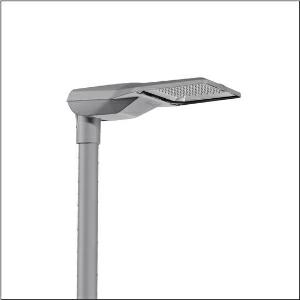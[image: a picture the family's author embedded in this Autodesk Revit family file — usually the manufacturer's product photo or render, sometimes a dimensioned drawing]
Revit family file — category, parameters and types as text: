
# Revit family: streetlight_sl_21_iq_midi___st0_8a_5xe3c31g08nb_0abe
name_source: partatom
category: Lighting Fixtures
units: mm (PartAtom-declared; Revit-internal decimal feet)

## family parameters
Cut with Voids When Loaded = No
Host = Face
Light Source = No
Part Type = Normal
Room Calculation Point = No
Round Connector Dimension = Use Diameter
Shared = No

## types (1)
- --- (1 x LED, 23230 lm, 155.5 W, 3000K)
    Apparent Load = 155 VA
    CIE Flux Codes = 41 75 97 100 100
    Color Rendering = 70
    Color Temperature = 3000K
    Default Elevation = 1800 mm
    Description = Streetlight SL 21 iQ midi, mast luminaire, primary light control with lens, of PMMA, primary optical cover: cover, of toughened safety glass, transparent, light distribution: ST0.8a, light emission: direct distribution, primary light characteristic: asymmetric, installation type: post-top, side-entry, LED, High Power LED, rated luminous flux: 23.230lm, luminous efficacy: 149lm/W, light colour: 730, colour temperature: 3000K, control: Street-Remote, Auto-Match, Temp-Guard, Lumen-Switch, Night-Set, Smart-Wire, Light-Fading, Desk-Remote (wireless, voltage-free reading and setting of iQ features in the workshop via application-optimized NFC function/RFID function), optimised constant luminous flux control (CLO 2.0), presetting dimming linear, mains connection: 230..240V, AC, 50/60Hz, start of lifetime: 156W, end of service life: 162W, reduction: 69W, luminaire housing, of diecast aluminium, powder-coated, Siteco® metallic grey (DB 702S), corrosivity category C5 mid according to DIN EN ISO 12944, please order mast flange separately, inclination adjustable: 0°, 5°, 10°, 15°, sealing non-destructively replaceable, multi-level sealing system, length: 644mm, width: 335mm, height: 110mm, mast flange for spigot size: 42mm (side-entry): 5XC10008XM4, 60/48mm (side-entry/post-top): 5XC10108XM2, 76/60mm (side-entry/post-top): 5XC10108XM1, protection rating (complete): IP66, insulation class (complete): insulation class II (safety insulation), certification: CE, ENEC, ENEC+, VDE, impact resistance: IK09, permissible operating ambient temperature for outdoor applications: -40..+50°C, standard-compliant lighting for roads and squares, packaging unit: 1 piece

Light Distribution: ST0.8a
    Height = 111 mm
    Lamp = 1 x LED
    Lamp Light Flux = 23230 lm
    Lamp Power = 155.5 W
    Lamp count = 1
    Length = 644 mm
    Luminous efficacy = 149 lm/W
    Manufacturer = Siteco
    ModVariant = No
    Model = 5XE3C31G08NB
    Number of Poles = 1
    OnlyDefault = Yes
    Power Factor = 1
    Product Name = Streetlight SL 21 iQ midi | ST0.8a
    Product group = mast luminaire | pylon top
    ProductGroupID = 6100
    Protection Class = Protection class II
    Protection Degree = IP 66
    RLX_Detail_Level = 1
    RLX_Emergency_Light_Flux = 0 lm
    RLX_Emergency_Type = 0
    RLX_Emergency_Type_DB = No
    RlxData = <blob elided: 91649 chars, md5=258139a9>
    Socket = socket
    Standby Power = 0 W
    System Light Flux = 23230 lm
    System Power = 155 W
    Type Comments = factory setting: luminous flux: 100 % | dim-lin: 254 | 823 mA
    Type Image = l_1004298.jpg
    URL = http://relux.com
    VarID = @adj_101385
    Voltage = 0 V
    Weight = 0.00 kg
    Width = 336 mm

## geometry (parser evidence)
native form markers: Blend x4, Sweep x11
no freeform markers — native parametric forms only
